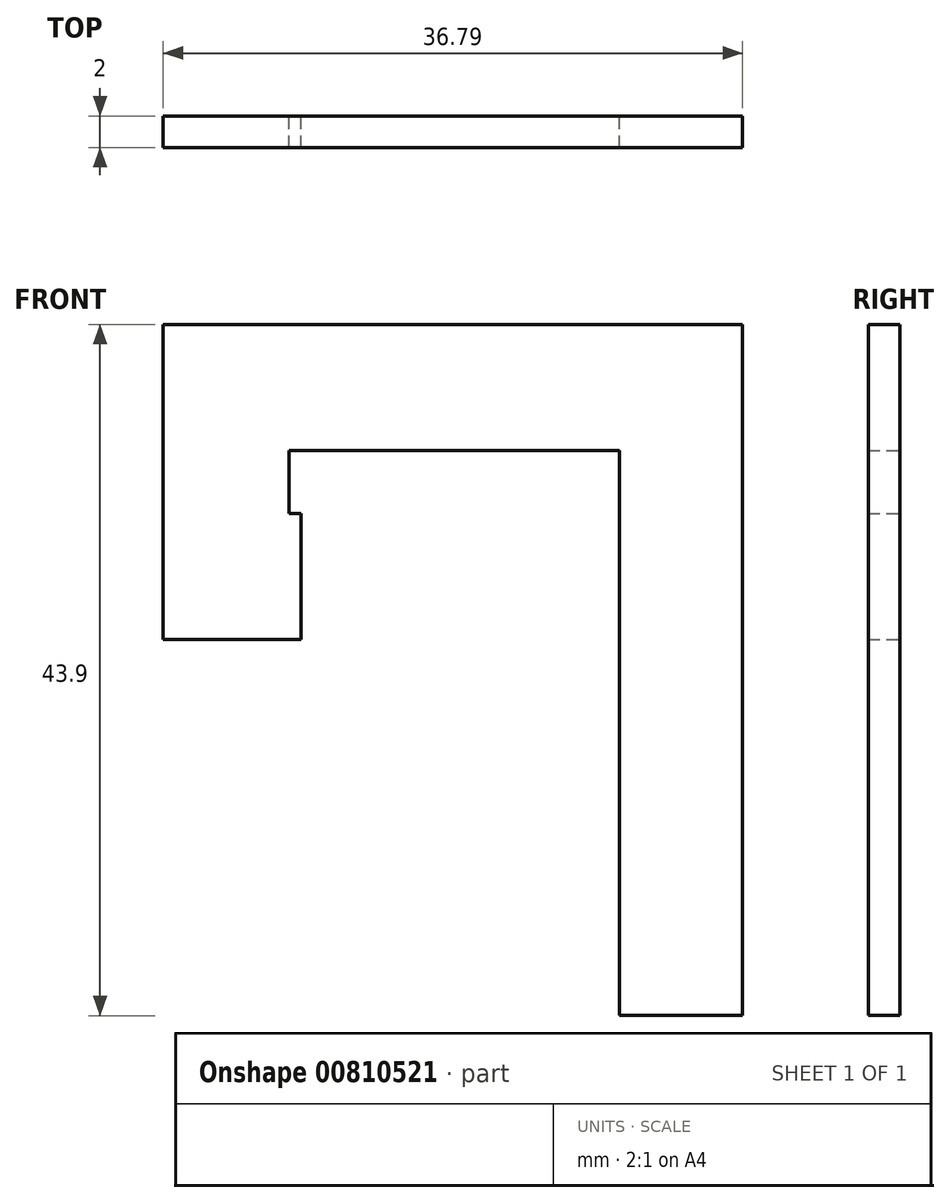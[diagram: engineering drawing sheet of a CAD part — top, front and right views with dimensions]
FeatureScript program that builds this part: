
annotation { "Feature Type Name" : "Feature", "Feature Type Description" : "" }
export const myFeature = defineFeature(function(context is Context, id is Id, definition is map)
    precondition{}
    {
        {
            var Q0;
            Q0=qCreatedBy(makeId("Front.planeOp"),FACE);
            var sketch = newSketch(context, id + "F0", { "sketchPlane" : qUnion([Q0])});
            skLineSegment(sketch, "E0", {"start": v(43.64, 19.4) * mm, "end": v(22.64, 19.4) * mm});
            skLineSegment(sketch, "E1", {"start": v(22.64, 19.4) * mm, "end": v(22.64, 7.4) * mm});
            skLineSegment(sketch, "E2", {"start": v(22.64, 7.4) * mm, "end": v(14.64, 7.4) * mm});
            skLineSegment(sketch, "E3", {"start": v(14.64, 7.4) * mm, "end": v(14.64, 27.4) * mm});
            skLineSegment(sketch, "E4", {"start": v(14.64, 27.4) * mm, "end": v(43.64, 27.4) * mm});
            skLineSegment(sketch, "E5", {"start": v(22.64, 15.4) * mm, "end": v(23.39, 15.4) * mm});
            skLineSegment(sketch, "E6", {"start": v(22.64, 7.4) * mm, "end": v(23.39, 7.4) * mm});
            skLineSegment(sketch, "E7", {"start": v(23.39, 15.4) * mm, "end": v(23.39, 7.4) * mm});
            skLineSegment(sketch, "E8", {"start": v(43.64, 27.4) * mm, "end": v(43.64, -16.5) * mm});
            skLineSegment(sketch, "E9", {"start": v(43.64, -16.5) * mm, "end": v(51.43, -16.5) * mm});
            skLineSegment(sketch, "E10", {"start": v(51.43, -16.5) * mm, "end": v(51.43, 27.4) * mm});
            skLineSegment(sketch, "E11", {"start": v(51.43, 27.4) * mm, "end": v(43.64, 27.4) * mm});
            skSolve(sketch);
        }
        {
            var Q0;
            {var subQ3=sQuery(id+"F0.wireOp",EDGE,"E0");Q0=makeQuery(id+"F0.imprint","IMPRINT",FACE,{"disambiguationData":[TD([[makeQuery(id+"F0.imprint","IMPRINT",EDGE,{"derivedFrom":subQ3}),-1.0]])]});}
            var Q1;
            {var subQ2=sQuery(id+"F0.wireOp",EDGE,"E5");Q1=makeQuery(id+"F0.imprint","IMPRINT",FACE,{"disambiguationData":[TD([[makeQuery(id+"F0.imprint","IMPRINT",EDGE,{"derivedFrom":subQ2}),-1.0]])]});}
            var Q2;
            {var subQ0=sQuery(id+"F0.wireOp",EDGE,"E9");Q2=makeQuery(id+"F0.imprint","IMPRINT",FACE,{"disambiguationData":[TD([[makeQuery(id+"F0.imprint","IMPRINT",EDGE,{"derivedFrom":subQ0}),1.0]])]});}
            extrude(context, id + "F1", {"entities" : qUnion([Q0, Q1, Q2]), "depth" : 2 * mm, "offsetDistance" : 25 * mm});
        }
    });
